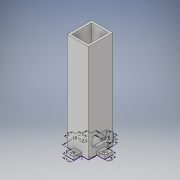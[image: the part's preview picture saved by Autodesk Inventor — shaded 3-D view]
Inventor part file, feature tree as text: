
AUTODESK INVENTOR PART (.ipt)
format: ipt  version: 2019 (Build 230136000, 136)  size: 191,488 bytes
history: native  units: mm
features: extrude x5, sketch x4, other x1
ambient origin geometry x8: Origin, YZ Plane, XZ Plane, XY Plane, X Axis, Y Axis, Z Axis, Center Point
bodies: Body1 (feature_tree)
feature tree (10):
  other  "Sólido1"
  sketch  "Boceto1"  dims[d0=14.0mm d1=16.0mm]
  extrude  "Extrusión1"  Depth=16.0mm
  extrude  "Extrusión2"  Depth=12.0mm
  extrude  "Extrusión3"  Depth=5.0mm
  extrude  "Extrusión4"  Depth=2.0mm
  extrude  "Extrusión5"  Depth=2.5mm
  sketch  "Boceto2"  dims[d2=10.0mm d3=12.0mm]
  sketch  "Boceto3"  dims[d4=2.5mm d5=5.0mm]
  sketch  "Boceto4"  dims[d6=5.0mm d7=2.0mm d8=2.5mm d9=5.0mm d10=5.0mm d11=2.0mm d12=2.5mm d13=5.0mm d14=5.0mm d15=2.0mm d16=2.5mm d17=5.0mm d18=5.0mm d19=2.0mm d20=2.0mm d21=0.0mm d22=62.0mm d23=0.0mm d24=2.0mm d25=0.0mm d26=2.0mm d27=0.0mm d28=11.0mm d29=13.0mm d30=28.0mm d31=0.0mm]
